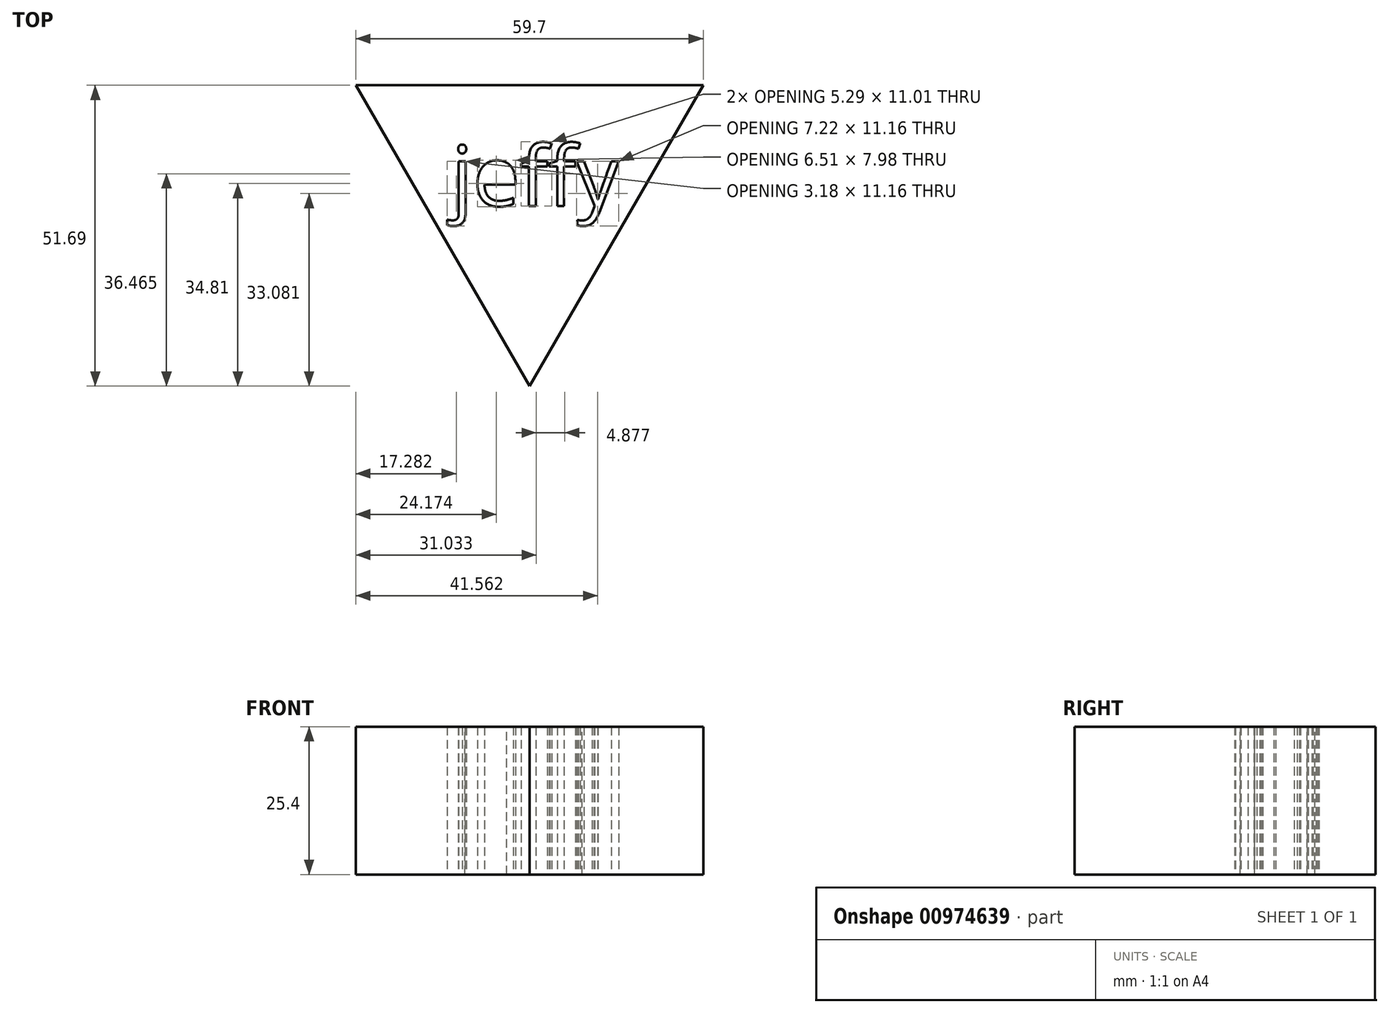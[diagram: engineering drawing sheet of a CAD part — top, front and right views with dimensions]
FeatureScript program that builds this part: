
annotation { "Feature Type Name" : "Feature", "Feature Type Description" : "" }
export const myFeature = defineFeature(function(context is Context, id is Id, definition is map)
    precondition{}
    {
        {
            var Q0;
            Q0=qCreatedBy(makeId("Top.planeOp"),FACE);
            var sketch = newSketch(context, id + "F0", { "sketchPlane" : qUnion([Q0])});
            skCircle(sketch, "E0.cCircle", {"center": v(0, 0) * mm, "radius": 17.23 * mm, "construction": true});
            skLineSegment(sketch, "E0.0", {"start": v(-29.85, 17.23) * mm, "end": v(29.85, 17.23) * mm});
            skLineSegment(sketch, "E0.1", {"start": v(29.85, 17.23) * mm, "end": v(0, -34.46) * mm});
            skLineSegment(sketch, "E0.2", {"start": v(0, -34.46) * mm, "end": v(-29.85, 17.23) * mm});
            skPoint(sketch, "E0.0.midPoint", {"position": v(0, 17.23) * mm});
            skText(sketch, "E1", { "text": "jeffy\n", "fontName": "OpenSans-Regular.ttf"});
            const initialGuessF0  = {"E1": [-0.01338, -0.0035, 1, 0, 0.01036]};
            skSetInitialGuess(sketch, initialGuessF0);
            skSolve(sketch);
        }
        {
            var Q0;
            Q0 = qSketchRegion(id + "F0", true);
            extrude(context, id + "F1", {"entities" : qUnion([Q0]), "depth" : 25.4 * mm, "offsetDistance" : 25.4 * mm});
        }
    });
